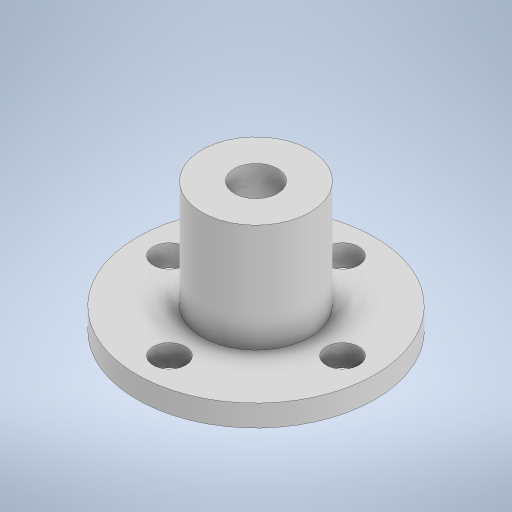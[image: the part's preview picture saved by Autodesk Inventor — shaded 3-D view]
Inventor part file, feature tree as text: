
AUTODESK INVENTOR PART (.ipt)
format: ipt  version: 2023.1 (Build 271208000, 208)  size: 252,416 bytes
history: native  units: mm
features: sketch x3, extrude x2, hole x1
ambient origin geometry x8: Origin, YZ Plane, XZ Plane, XY Plane, X Axis, Y Axis, Z Axis, Center Point
bodies: Solid1 (feature_tree)
feature tree (6):
  extrude  "Extrusion1"  Depth=2.0mm TaperAngle=0.0deg
  extrude  "Extrusion2"  Depth=10.0mm TaperAngle=0.0deg
  hole  "Hole1"  [1 undecoded]
  sketch  "Sketch1"  dims[d0=22.0mm d1=2.0mm d2=0.0mm]
  sketch  "Sketch2"  dims[d3=10.0mm d4=10.0mm d5=0.0mm]
  sketch  "Sketch3"  dims[d6=4.0mm d7=4.0mm d8=6.0mm d9=4.0mm d10=2.0mm d11=90.0deg d12=8.0mm d13=20.594885mm d15=3.0mm d16=40.0mm d18=360.0deg]
note: 1 required parameter value undecoded (feature->parameter linkage not recoverable at this tier; creation-order binding heuristic only, values carry confidence <= 0.55)
